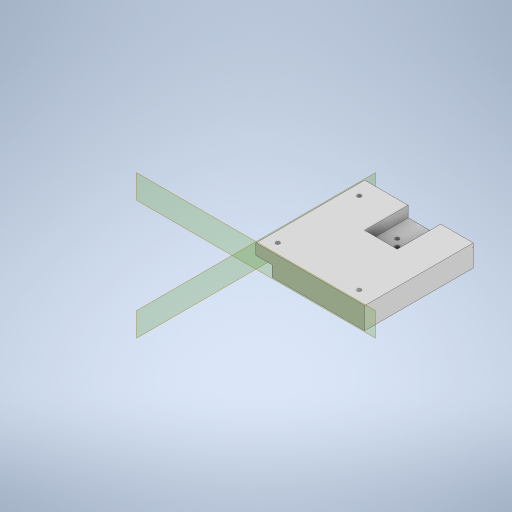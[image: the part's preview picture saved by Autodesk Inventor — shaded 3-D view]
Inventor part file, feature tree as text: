
AUTODESK INVENTOR PART (.ipt)
format: ipt  version: 2023 (Build 270158000, 158)  size: 364,544 bytes
history: native  units: mm
features: sketch x8, extrude x5, other x4, hole x3, plane x2, split x2
ambient origin geometry x8: Origin, YZ Plane, XZ Plane, XY Plane, X Axis, Y Axis, Z Axis, Center Point
bodies: Body1 (feature_tree)
feature tree (24):
  other  "Sólido1"
  other  "Anotaciones"
  extrude  "Extrusión1"  Depth=200.0mm
  extrude  "Extrusión2"  Depth=10.0mm TaperAngle=0.0deg
  extrude  "Extrusión3"  Depth=20.0mm
  hole  "Agujero1"  [1 undecoded]
  extrude  "Extrusión4"  Depth=10.0mm
  plane  "Plano de trabajo1"
  plane  "Plano de trabajo2"
  hole  "Agujero2"  [1 undecoded]
  extrude  "Extrusión5"  Depth=10.0mm TaperAngle=0.0deg
  hole  "Agujero3"  [1 undecoded]
  split  "Dividir3"
  split  "Dividir4"
  sketch  "Boceto1"  dims[d0=200.0mm d1=200.0mm]
  sketch  "Boceto2"  dims[d2=20.0mm d3=0.0mm]
  sketch  "Boceto3"  dims[d4=20.0mm d5=20.0mm d6=30.0mm d7=30.0mm d8=20.0mm d9=35.0mm d10=35.0mm d11=60.0mm d12=10.0mm d13=0.0mm]
  sketch  "Boceto4"  dims[d14=20.0mm d15=0.0mm]
  sketch  "Boceto5"  dims[d16=3.5mm d18=1.75mm d19=1.75mm d20=1.75mm d21=1.75mm d22=10.0mm d23=10.0mm d25=20.0mm]
  sketch  "Boceto7"  dims[d26=40.0mm d27=40.0mm]
  sketch  "Boceto8"  dims[d28=3.5mm d29=6.0mm d30=4.0mm d31=2.0mm d32=90.0deg d33=8.0mm d34=20.594885mm d38=10.0mm]
  sketch  "Boceto9"  dims[d39=10.0mm d40=40.0mm d41=10.0mm d42=0.0mm d52=3.5mm d54=10.0mm d55=10.0mm d56=3.5mm d57=6.0mm d58=4.0mm d59=2.0mm d60=90.0deg d61=8.0mm d62=20.594885mm d63=30.0mm d64=30.0mm d65=10.0mm d66=0.0mm d67=3.5mm d68=15.0mm d69=10.0mm d70=45.0deg d71=45.0deg d72=3.5mm d73=6.0mm d74=4.0mm d75=2.0mm d76=90.0deg d77=8.0mm d78=20.594885mm d43=6.672192mm d44=4.931866mm d45=30.0mm d46=5.890777mm d47=4.508932mm d48=30.0mm d83=0.5mm d84=0.872665mm d85=0.5mm d86=0.872665mm]
  other  "Cota lineal 1"
  other  "Cota lineal 2"
note: 3 required parameter values undecoded (feature->parameter linkage not recoverable at this tier; creation-order binding heuristic only, values carry confidence <= 0.55)
